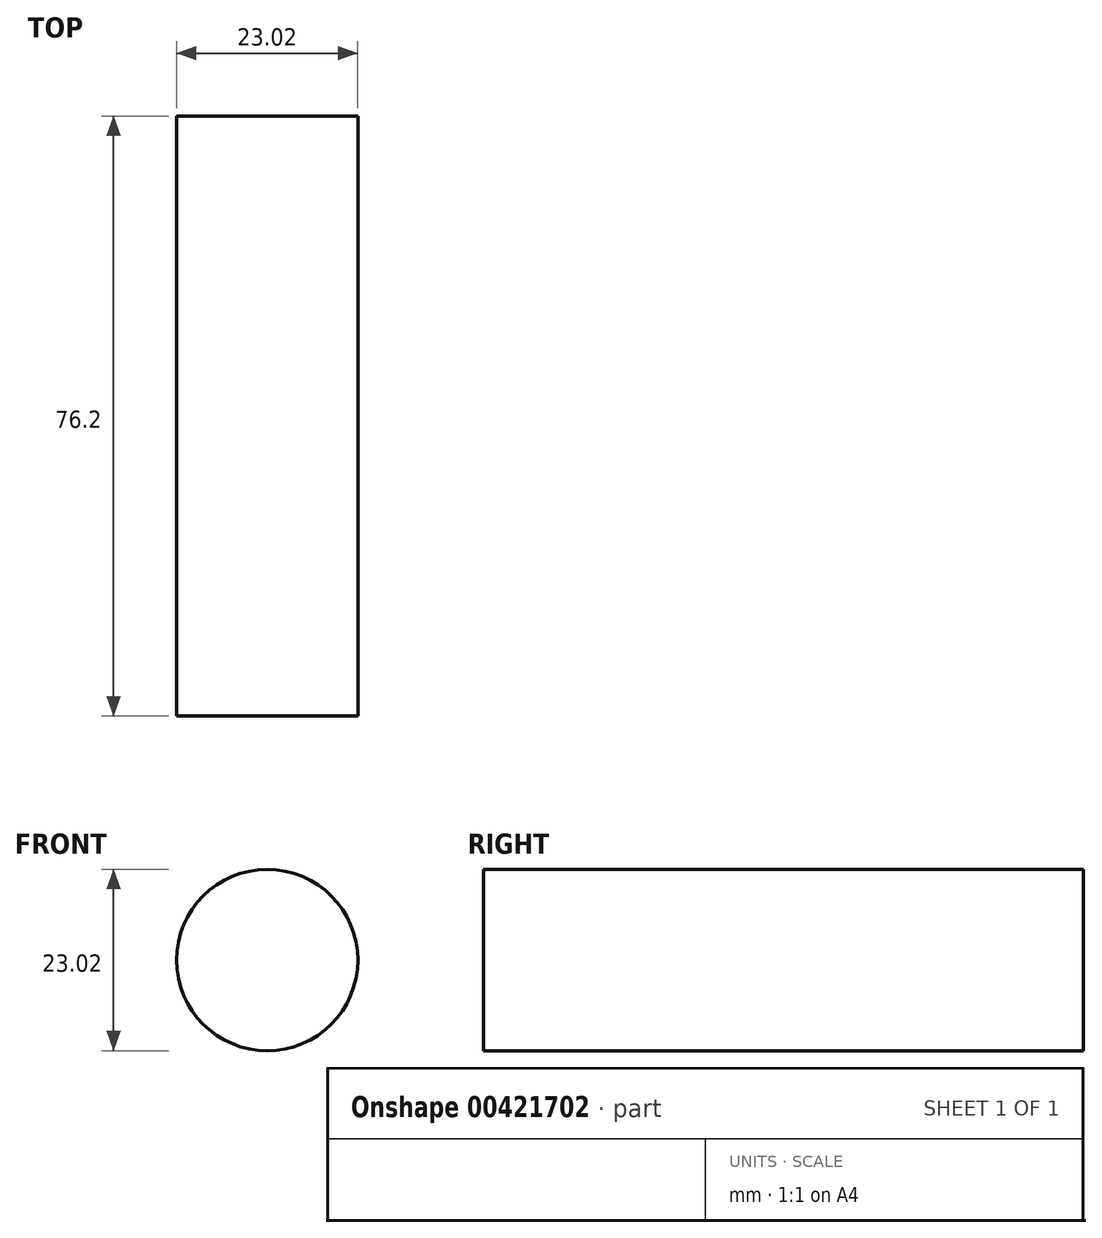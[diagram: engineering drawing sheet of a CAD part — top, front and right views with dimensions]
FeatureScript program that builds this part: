
annotation { "Feature Type Name" : "Feature", "Feature Type Description" : "" }
export const myFeature = defineFeature(function(context is Context, id is Id, definition is map)
    precondition{}
    {
        {
            var Q0;
            Q0=qCreatedBy(makeId("Front.planeOp"),FACE);
            var sketch = newSketch(context, id + "F0", { "sketchPlane" : qUnion([Q0])});
            skCircle(sketch, "E0", {"center": v(0, 0) * mm, "radius": 11.51 * mm});
            skSolve(sketch);
        }
        {
            var Q0;
            Q0=makeQuery(id+"F0.imprint","IMPRINT",FACE,{"disambiguationData":[TD([[makeQuery(id+"F0.imprint","IMPRINT",EDGE,{"derivedFrom":sQuery(id+"F0.wireOp",EDGE,"E0")}),1.0]])]});
            extrude(context, id + "F1", {"entities" : qUnion([Q0]), "depth" : 76.2 * mm});
        }
    });
